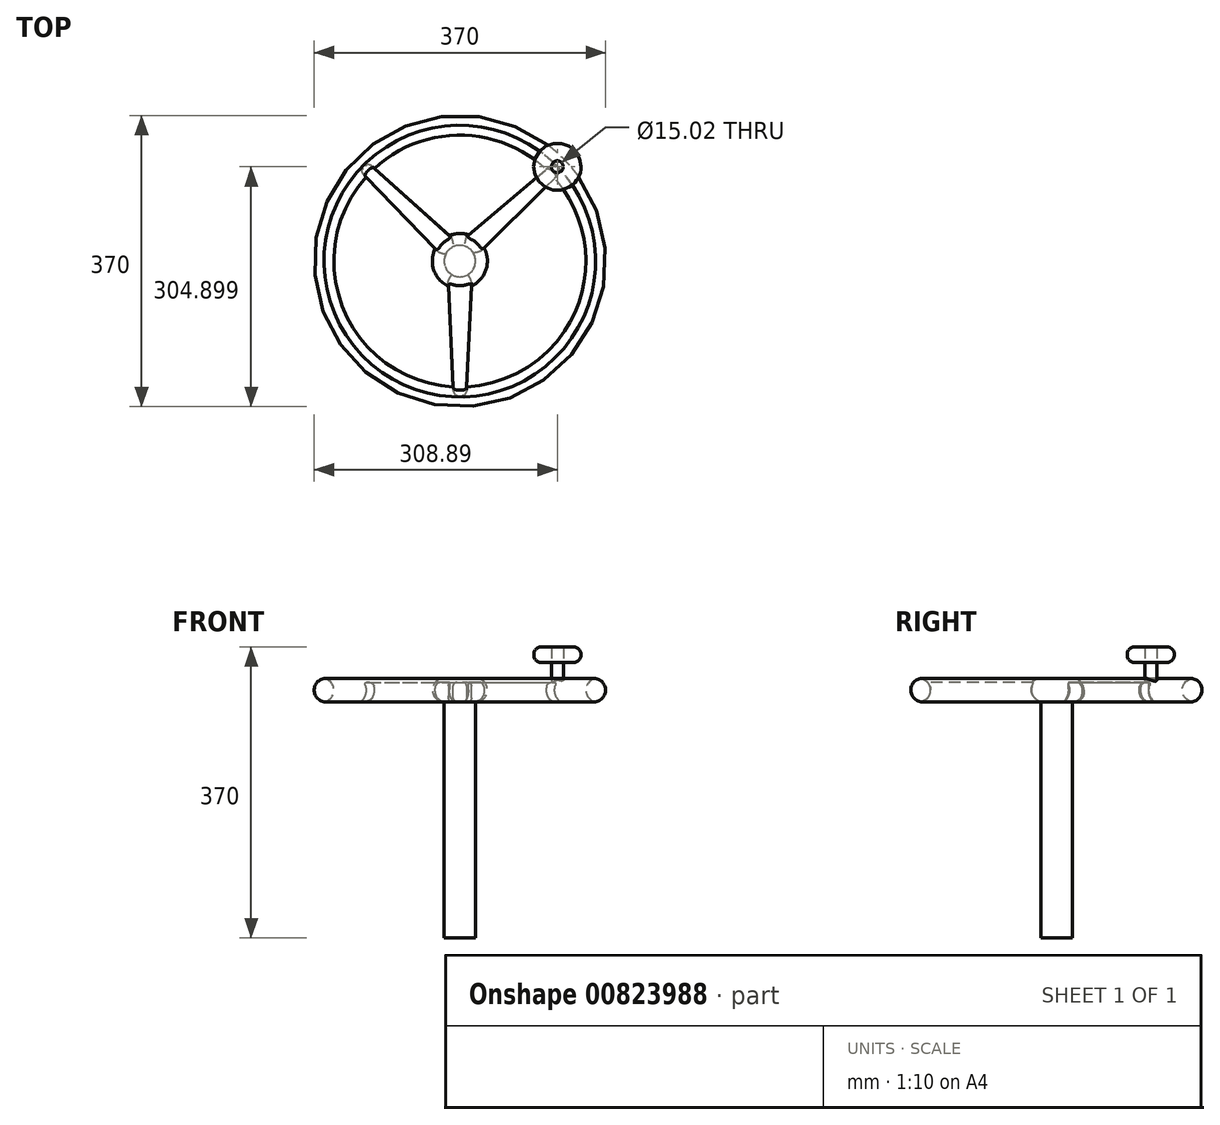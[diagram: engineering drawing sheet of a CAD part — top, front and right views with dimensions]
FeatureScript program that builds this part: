
annotation { "Feature Type Name" : "Feature", "Feature Type Description" : "" }
export const myFeature = defineFeature(function(context is Context, id is Id, definition is map)
    precondition{}
    {
        {
            var Q0;
            Q0=qCreatedBy(makeId("Top.planeOp"),FACE);
            var sketch = newSketch(context, id + "F0", { "sketchPlane" : qUnion([Q0])});
            skCircle(sketch, "E0", {"center": v(0, 0) * mm, "radius": 185 * mm});
            skCircle(sketch, "E1", {"center": v(0, 0) * mm, "radius": 35 * mm});
            skLineSegment(sketch, "E2", {"start": v(-108.34, 117.74) * mm, "end": v(-13.45, 32.31) * mm});
            skLineSegment(sketch, "E3.MirrorCS", {"start": v(-119.25, 106.67) * mm, "end": v(-30.44, 14.72) * mm});
            skLineSegment(sketch, "E4", {"start": v(11.28, 33.13) * mm, "end": v(109.6, 116.57) * mm});
            skLineSegment(sketch, "E5.MirrorCS", {"start": v(28.6, 14.25) * mm, "end": v(120.5, 105.25) * mm});
            skLineSegment(sketch, "E6", {"start": v(-14.58, -31.82) * mm, "end": v(-8.8, -159.76) * mm});
            skLineSegment(sketch, "E7.MirrorCS", {"start": v(14.58, -31.82) * mm, "end": v(8.8, -159.76) * mm});
            skArc(sketch, "E8", {"start": v(-108.34, 117.74) * mm, "mid": v(-113.93, 112.34) * mm, "end": v(-119.25, 106.67) * mm});
            skArc(sketch, "E9", {"start": v(-119.25, 106.67) * mm, "mid": v(6.92, -159.85) * mm, "end": v(109.6, 116.57) * mm});
            skArc(sketch, "E10", {"start": v(109.6, 116.57) * mm, "mid": v(0.86, 160) * mm, "end": v(-108.34, 117.74) * mm});
            skLineSegment(sketch, "E11", {"start": v(109.6, 116.57) * mm, "end": v(109.6, 116.57) * mm});
            skSolve(sketch);
        }
        {
            var Q0;
            Q0 = qSketchRegion(id + "F0", true);
            extrude(context, id + "F1", {"entities" : qUnion([Q0]), "depth" : 30 * mm, "offsetDistance" : 25 * mm});
        }
        {
            var Q0;
            {var subQ0=sQuery(id+"F0.wireOp",EDGE,"E2");Q0=makeQuery(id+"F0.imprint","IMPRINT",FACE,{"disambiguationData":[TD([[makeQuery(id+"F0.imprint","IMPRINT",EDGE,{"derivedFrom":subQ0}),-1.0]])]});}
            var Q1;
            {var subQ0=sQuery(id+"F0.wireOp",EDGE,"E4");Q1=makeQuery(id+"F0.imprint","IMPRINT",FACE,{"disambiguationData":[TD([[makeQuery(id+"F0.imprint","IMPRINT",EDGE,{"derivedFrom":subQ0}),-1.0]])]});}
            var Q2;
            {var subQ0=sQuery(id+"F0.wireOp",EDGE,"E6");Q2=makeQuery(id+"F0.imprint","IMPRINT",FACE,{"disambiguationData":[TD([[makeQuery(id+"F0.imprint","IMPRINT",EDGE,{"derivedFrom":subQ0}),1.0]])]});}
            extrude(context, id + "F2", {"entities" : qUnion([Q0, Q1, Q2]), "operationType" : NewBodyOperationType.ADD, "depth" : 25 * mm, "offsetDistance" : 25 * mm});
        }
        {
            var Q0;
            {var subQ0=sQuery(id+"F0.wireOp",EDGE,"E1");var subQ4=makeQuery(id+"F0.imprint","INTERSECT",VERTEX,{"derivedFrom":[subQ0,sQuery(id+"F0.wireOp",EDGE,"E4")]});Q0=makeQuery(id+"F0.imprint","IMPRINT",FACE,{"disambiguationData":[TD([[makeQuery(id+"F0.imprint","IMPRINT",EDGE,{"disambiguationData":[TD([[subQ4,1.0]])],"derivedFrom":subQ0}),1.0]])]});}
            extrude(context, id + "F3", {"entities" : qUnion([Q0]), "operationType" : NewBodyOperationType.ADD, "depth" : 30 * mm, "offsetDistance" : 25 * mm});
        }
        {
            var Q0;
            Q0=makeQuery(id+"F1.opExtrude","CAP_FACE",FACE,{"disambiguationData":[OSD([sQuery(id+"F0.wireOp",EDGE,"E0"),sQuery(id+"F0.wireOp",EDGE,"E8"),sQuery(id+"F0.wireOp",EDGE,"E9"),sQuery(id+"F0.wireOp",EDGE,"E10")])],"isStart":false});
            var sketch = newSketch(context, id + "F4", { "sketchPlane" : qUnion([Q0])});
            skCircle(sketch, "E12", {"center": v(123.9, 119.9) * mm, "radius": 7.5 * mm});
            skSolve(sketch);
        }
        {
            var Q0;
            {var subQ0=sQuery(id+"F4.wireOp",EDGE,"E12");var subQ1=sQuery(id+"F0.wireOp",EDGE,"E10");var subQ2=sQuery(id+"F0.wireOp",EDGE,"E9");var subQ3=sQuery(id+"F0.wireOp",EDGE,"E8");var subQ4=makeQuery(id+"FWXwjLr2z3z57AX_1.opFillet","BLEND_EDGE",EDGE,{"blendedFrom":[makeQuery(id+"F1.opExtrude","CAP_EDGE",EDGE,{"disambiguationData":[OSD([subQ3,subQ2,subQ1])],"isStart":false}),makeQuery(id+"F1.opExtrude","CAP_FACE",FACE,{"disambiguationData":[OSD([sQuery(id+"F0.wireOp",EDGE,"E0"),subQ3,subQ2,subQ1])],"isStart":false})],"blendedInto":[makeQuery(id+"F1.opExtrude","CAP_FACE",FACE,{"disambiguationData":[OSD([sQuery(id+"F0.wireOp",EDGE,"E0"),subQ3,subQ2,subQ1])],"isStart":false})]});var subQ5=makeQuery(id+"F4.imprint","INTERSECT",VERTEX,{"disambiguationData":[OD(0.0)],"derivedFrom":[subQ4,subQ0]});Q0=makeQuery(id+"F4.imprint","IMPRINT",FACE,{"disambiguationData":[TD([[makeQuery(id+"F4.imprint","IMPRINT",EDGE,{"disambiguationData":[TD([[subQ5,1.0]])],"derivedFrom":subQ0}),1.0]])]});}
            var Q1;
            Q1=sQuery(id+"F4.wireOp",EDGE,"E12");
            extrude(context, id + "F5", {"entities" : qUnion([Q0]), "operationType" : NewBodyOperationType.ADD, "surfaceEntities" : qUnion([Q1]), "depth" : 20 * mm, "offsetDistance" : 25 * mm});
        }
        {
            var Q0;
            Q0=makeQuery(id+"F5.opExtrude","CAP_FACE",FACE,{"disambiguationData":[OSD([sQuery(id+"F0.wireOp",EDGE,"E0"),sQuery(id+"F0.wireOp",EDGE,"E8"),sQuery(id+"F0.wireOp",EDGE,"E9"),sQuery(id+"F0.wireOp",EDGE,"E10"),sQuery(id+"F4.wireOp",EDGE,"E12")])],"isStart":false});
            var sketch = newSketch(context, id + "F6", { "sketchPlane" : qUnion([Q0])});
            skCircle(sketch, "E13", {"center": v(123.9, 119.9) * mm, "radius": 30 * mm});
            skSolve(sketch);
        }
        {
            var Q0;
            Q0=makeQuery(id+"F6.imprint","IMPRINT",FACE,{"disambiguationData":[TD([[makeQuery(id+"F6.imprint","IMPRINT",EDGE,{"derivedFrom":sQuery(id+"F6.wireOp",EDGE,"E13")}),1.0]])]});
            var Q1;
            Q1=sQuery(id+"F6.wireOp",EDGE,"E13");
            extrude(context, id + "F7", {"entities" : qUnion([Q0]), "surfaceEntities" : qUnion([Q1]), "depth" : 20 * mm, "offsetDistance" : 25 * mm});
        }
        {
            var Q0;
            Q0=makeQuery(id+"F5.opExtrude","CAP_FACE",FACE,{"disambiguationData":[OSD([sQuery(id+"F0.wireOp",EDGE,"E0"),sQuery(id+"F0.wireOp",EDGE,"E8"),sQuery(id+"F0.wireOp",EDGE,"E9"),sQuery(id+"F0.wireOp",EDGE,"E10"),sQuery(id+"F4.wireOp",EDGE,"E12")])],"isStart":false});
            extrude(context, id + "F8", {"entities" : qUnion([Q0]), "depth" : 20 * mm, "offsetDistance" : 25 * mm});
        }
        {
            var Q0;
            Q0=makeQuery(id+"F7.opExtrude","CAP_EDGE",EDGE,{"disambiguationData":[OSD([sQuery(id+"F6.wireOp",EDGE,"E13")])],"isStart":false});
            fillet(context, id + "F9", {"entities" : qUnion([Q0]), "radius" : 10 * mm, "tangentPropagation" : true, "allowEdgeOverflow" : false});
        }
        {
            var Q0;
            Q0=makeQuery(id+"F7.opExtrude","CAP_EDGE",EDGE,{"disambiguationData":[OSD([sQuery(id+"F6.wireOp",EDGE,"E13")])],"isStart":true});
            fillet(context, id + "F10", {"entities" : qUnion([Q0]), "radius" : 10 * mm, "tangentPropagation" : true, "allowEdgeOverflow" : false});
        }
        {
            var Q0;
            Q0=makeQuery(id+"F1.opExtrude","CAP_EDGE",EDGE,{"disambiguationData":[OSD([sQuery(id+"F0.wireOp",EDGE,"E8"),sQuery(id+"F0.wireOp",EDGE,"E9"),sQuery(id+"F0.wireOp",EDGE,"E10")])],"isStart":false});
            fillet(context, id + "F11", {"entities" : qUnion([Q0]), "radius" : 15 * mm, "tangentPropagation" : true, "allowEdgeOverflow" : false});
        }
        {
            var Q0;
            {var subQ0=sQuery(id+"F0.wireOp",EDGE,"E8");var subQ1=sQuery(id+"F0.wireOp",EDGE,"E3.MirrorCS");var subQ3=sQuery(id+"F0.wireOp",EDGE,"E9");var subQ4=sQuery(id+"F0.wireOp",EDGE,"E10");Q0=makeQuery(id+"F2.boolean.opBoolean","SPLIT",EDGE,{"disambiguationData":[TD([makeQuery(id+"F2.opExtrude","SWEPT_FACE",FACE,{"disambiguationData":[OSD([subQ1])]})])],"derivedFrom":makeQuery(id+"F1.opExtrude","CAP_EDGE",EDGE,{"disambiguationData":[OSD([subQ0,subQ3,subQ4])],"isStart":true})});}
            fillet(context, id + "F12", {"entities" : qUnion([Q0]), "radius" : 15 * mm, "tangentPropagation" : true, "allowEdgeOverflow" : false});
        }
        {
            var Q0;
            Q0=makeQuery(id+"F1.opExtrude","CAP_EDGE",EDGE,{"disambiguationData":[OSD([sQuery(id+"F0.wireOp",EDGE,"E0")])],"isStart":false});
            fillet(context, id + "F13", {"entities" : qUnion([Q0]), "radius" : 15 * mm, "tangentPropagation" : true, "allowEdgeOverflow" : false});
        }
        {
            var Q0;
            {var subQ0=sQuery(id+"F0.wireOp",EDGE,"E8");var subQ1=sQuery(id+"F0.wireOp",EDGE,"E2");var subQ3=sQuery(id+"F0.wireOp",EDGE,"E9");var subQ5=sQuery(id+"F0.wireOp",EDGE,"E10");Q0=makeQuery(id+"F2.boolean.opBoolean","SPLIT",EDGE,{"disambiguationData":[TD([makeQuery(id+"F2.opExtrude","SWEPT_FACE",FACE,{"disambiguationData":[OSD([subQ1])]})])],"derivedFrom":makeQuery(id+"F1.opExtrude","CAP_EDGE",EDGE,{"disambiguationData":[OSD([subQ0,subQ3,subQ5])],"isStart":true})});}
            fillet(context, id + "F14", {"entities" : qUnion([Q0]), "radius" : 15 * mm, "tangentPropagation" : true, "allowEdgeOverflow" : false});
        }
        {
            var Q0;
            {var subQ0=sQuery(id+"F0.wireOp",EDGE,"E8");var subQ2=sQuery(id+"F0.wireOp",EDGE,"E9");var subQ3=sQuery(id+"F0.wireOp",EDGE,"E5.MirrorCS");var subQ4=sQuery(id+"F0.wireOp",EDGE,"E10");Q0=makeQuery(id+"F2.boolean.opBoolean","SPLIT",EDGE,{"disambiguationData":[TD([makeQuery(id+"F2.opExtrude","SWEPT_FACE",FACE,{"disambiguationData":[OSD([subQ3])]})])],"derivedFrom":makeQuery(id+"F1.opExtrude","CAP_EDGE",EDGE,{"disambiguationData":[OSD([subQ0,subQ2,subQ4])],"isStart":true})});}
            fillet(context, id + "F15", {"entities" : qUnion([Q0]), "radius" : 15 * mm, "tangentPropagation" : true, "allowEdgeOverflow" : false});
        }
        {
            var Q0;
            Q0=makeQuery(id+"F1.opExtrude","CAP_EDGE",EDGE,{"disambiguationData":[OSD([sQuery(id+"F0.wireOp",EDGE,"E0")])],"isStart":true});
            fillet(context, id + "F16", {"entities" : qUnion([Q0]), "radius" : 15 * mm, "tangentPropagation" : true, "allowEdgeOverflow" : false});
        }
        {
            var Q0;
            Q0=makeQuery(id+"F3.opExtrude","CAP_EDGE",EDGE,{"disambiguationData":[OSD([sQuery(id+"F0.wireOp",EDGE,"E1")])],"isStart":false});
            fillet(context, id + "F17", {"entities" : qUnion([Q0]), "radius" : 15 * mm, "tangentPropagation" : true, "allowEdgeOverflow" : false});
        }
        {
            var Q0;
            {var subQ2=sQuery(id+"F0.wireOp",EDGE,"E1");var subQ4=sQuery(id+"F0.wireOp",EDGE,"E3.MirrorCS");Q0=makeQuery(id+"F3.boolean.opBoolean","SPLIT",EDGE,{"disambiguationData":[TD([makeQuery(id+"F2.opExtrude","SWEPT_FACE",FACE,{"disambiguationData":[OSD([subQ4])]})])],"derivedFrom":makeQuery(id+"F3.opExtrude","CAP_EDGE",EDGE,{"disambiguationData":[OSD([subQ2])],"isStart":true})});}
            fillet(context, id + "F18", {"entities" : qUnion([Q0]), "radius" : 15 * mm, "tangentPropagation" : true, "allowEdgeOverflow" : false});
        }
        {
            var Q0;
            {var subQ2=sQuery(id+"F0.wireOp",EDGE,"E1");var subQ4=sQuery(id+"F0.wireOp",EDGE,"E5.MirrorCS");Q0=makeQuery(id+"F3.boolean.opBoolean","SPLIT",EDGE,{"disambiguationData":[TD([makeQuery(id+"F2.opExtrude","SWEPT_FACE",FACE,{"disambiguationData":[OSD([subQ4])]})])],"derivedFrom":makeQuery(id+"F3.opExtrude","CAP_EDGE",EDGE,{"disambiguationData":[OSD([subQ2])],"isStart":true})});}
            fillet(context, id + "F19", {"entities" : qUnion([Q0]), "radius" : 15 * mm, "tangentPropagation" : true, "allowEdgeOverflow" : false});
        }
        {
            var Q0;
            {var subQ1=sQuery(id+"F0.wireOp",EDGE,"E1");var subQ3=sQuery(id+"F0.wireOp",EDGE,"E2");Q0=makeQuery(id+"F3.boolean.opBoolean","SPLIT",EDGE,{"disambiguationData":[TD([makeQuery(id+"F2.opExtrude","SWEPT_FACE",FACE,{"disambiguationData":[OSD([subQ3])]})])],"derivedFrom":makeQuery(id+"F3.opExtrude","CAP_EDGE",EDGE,{"disambiguationData":[OSD([subQ1])],"isStart":true})});}
            fillet(context, id + "F20", {"entities" : qUnion([Q0]), "radius" : 12 * mm, "tangentPropagation" : true, "allowEdgeOverflow" : false});
        }
        {
            var Q0;
            Q0=makeQuery(id+"F2.opExtrude","CAP_EDGE",EDGE,{"disambiguationData":[OSD([sQuery(id+"F0.wireOp",EDGE,"E6")])],"isStart":false});
            var Q1;
            Q1=makeQuery(id+"F2.opExtrude","CAP_EDGE",EDGE,{"disambiguationData":[OSD([sQuery(id+"F0.wireOp",EDGE,"E7.MirrorCS")])],"isStart":false});
            var Q2;
            Q2=makeQuery(id+"F2.opExtrude","CAP_EDGE",EDGE,{"disambiguationData":[OSD([sQuery(id+"F0.wireOp",EDGE,"E3.MirrorCS")])],"isStart":false});
            var Q3;
            Q3=makeQuery(id+"F2.opExtrude","CAP_EDGE",EDGE,{"disambiguationData":[OSD([sQuery(id+"F0.wireOp",EDGE,"E2")])],"isStart":false});
            var Q4;
            Q4=makeQuery(id+"F2.opExtrude","CAP_EDGE",EDGE,{"disambiguationData":[OSD([sQuery(id+"F0.wireOp",EDGE,"E4")])],"isStart":false});
            var Q5;
            Q5=makeQuery(id+"F2.opExtrude","CAP_EDGE",EDGE,{"disambiguationData":[OSD([sQuery(id+"F0.wireOp",EDGE,"E5.MirrorCS")])],"isStart":false});
            fillet(context, id + "F21", {"entities" : qUnion([Q0, Q1, Q2, Q3, Q4, Q5]), "radius" : 5 * mm, "tangentPropagation" : true, "allowEdgeOverflow" : false});
        }
        {
            var Q0;
            Q0=makeQuery(id+"F2.opExtrude","CAP_EDGE",EDGE,{"disambiguationData":[OSD([sQuery(id+"F0.wireOp",EDGE,"E7.MirrorCS")])],"isStart":true});
            var Q1;
            Q1=makeQuery(id+"F2.opExtrude","CAP_EDGE",EDGE,{"disambiguationData":[OSD([sQuery(id+"F0.wireOp",EDGE,"E6")])],"isStart":true});
            var Q2;
            Q2=makeQuery(id+"F2.opExtrude","CAP_EDGE",EDGE,{"disambiguationData":[OSD([sQuery(id+"F0.wireOp",EDGE,"E5.MirrorCS")])],"isStart":true});
            var Q3;
            Q3=makeQuery(id+"F2.opExtrude","CAP_EDGE",EDGE,{"disambiguationData":[OSD([sQuery(id+"F0.wireOp",EDGE,"E4")])],"isStart":true});
            var Q4;
            Q4=makeQuery(id+"F2.opExtrude","CAP_EDGE",EDGE,{"disambiguationData":[OSD([sQuery(id+"F0.wireOp",EDGE,"E2")])],"isStart":true});
            var Q5;
            Q5=makeQuery(id+"F2.opExtrude","CAP_EDGE",EDGE,{"disambiguationData":[OSD([sQuery(id+"F0.wireOp",EDGE,"E3.MirrorCS")])],"isStart":true});
            fillet(context, id + "F22", {"entities" : qUnion([Q0, Q1, Q2, Q3, Q4, Q5]), "radius" : 5 * mm, "tangentPropagation" : true, "allowEdgeOverflow" : false});
        }
        {
            var Q0;
            {var subQ0=sQuery(id+"F0.wireOp",EDGE,"E1");var subQ4=makeQuery(id+"F0.imprint","INTERSECT",VERTEX,{"derivedFrom":[subQ0,sQuery(id+"F0.wireOp",EDGE,"E4")]});Q0=makeQuery(id+"F0.imprint","IMPRINT",FACE,{"disambiguationData":[TD([[makeQuery(id+"F0.imprint","IMPRINT",EDGE,{"disambiguationData":[TD([[subQ4,1.0]])],"derivedFrom":subQ0}),1.0]])]});}
            var sketch = newSketch(context, id + "F23", { "sketchPlane" : qUnion([Q0])});
            skCircle(sketch, "E14", {"center": v(0, 0) * mm, "radius": 20 * mm});
            skSolve(sketch);
        }
        {
            var Q0;
            Q0 = qSketchRegion(id + "F23", true);
            extrude(context, id + "F24", {"entities" : qUnion([Q0]), "operationType" : NewBodyOperationType.ADD, "oppositeDirection" : true, "depth" : 300 * mm, "offsetDistance" : 25 * mm});
        }
    });
